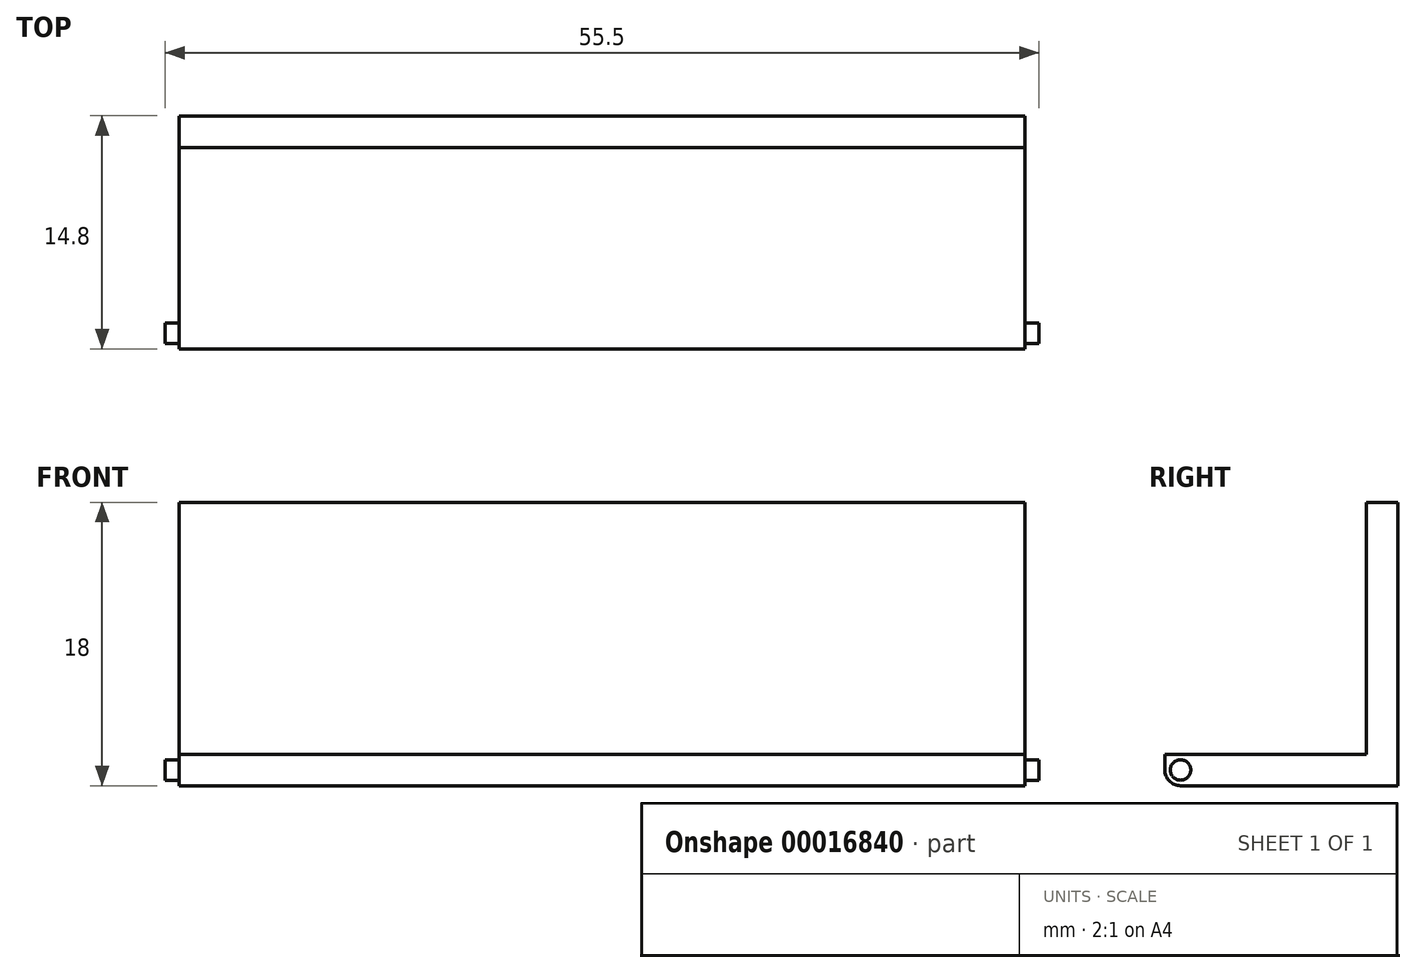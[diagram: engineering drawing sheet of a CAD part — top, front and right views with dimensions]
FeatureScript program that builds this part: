
annotation { "Feature Type Name" : "Feature", "Feature Type Description" : "" }
export const myFeature = defineFeature(function(context is Context, id is Id, definition is map)
    precondition{}
    {
        {
            var Q0;
            Q0=qCreatedBy(makeId("Top.planeOp"),FACE);
            var sketch = newSketch(context, id + "F0", { "sketchPlane" : qUnion([Q0])});
            skLineSegment(sketch, "E0.bottom", {"start": v(-78.46, -29.03) * mm, "end": v(-24.76, -29.03) * mm});
            skLineSegment(sketch, "E0.top", {"start": v(-78.46, -43.83) * mm, "end": v(-24.76, -43.83) * mm});
            skLineSegment(sketch, "E0.left", {"start": v(-78.46, -29.03) * mm, "end": v(-78.46, -43.83) * mm});
            skLineSegment(sketch, "E0.right", {"start": v(-24.76, -29.03) * mm, "end": v(-24.76, -43.83) * mm});
            skSolve(sketch);
        }
        {
            var Q0;
            Q0=makeQuery(id+"F0.imprint","IMPRINT",FACE,{"disambiguationData":[TD([[makeQuery(id+"F0.imprint","IMPRINT",EDGE,{"derivedFrom":sQuery(id+"F0.wireOp",EDGE,"E0.bottom")}),-1.0]])]});
            extrude(context, id + "F1", {"entities" : qUnion([Q0]), "depth" : 18 * mm});
        }
        {
            var Q0;
            Q0=makeQuery(id+"F1.opExtrude","CAP_FACE",FACE,{"disambiguationData":[OSD([sQuery(id+"F0.wireOp",EDGE,"E0.bottom"),sQuery(id+"F0.wireOp",EDGE,"E0.top"),sQuery(id+"F0.wireOp",EDGE,"E0.left"),sQuery(id+"F0.wireOp",EDGE,"E0.right")])],"isStart":false});
            shell(context, id + "F2", {"entities" : qUnion([Q0]), "thickness" : 2 * mm});
        }
        {
            var Q0;
            Q0=makeQuery(id+"F1.opExtrude","CAP_FACE",FACE,{"disambiguationData":[OSD([sQuery(id+"F0.wireOp",EDGE,"E0.bottom"),sQuery(id+"F0.wireOp",EDGE,"E0.top"),sQuery(id+"F0.wireOp",EDGE,"E0.left"),sQuery(id+"F0.wireOp",EDGE,"E0.right")])],"isStart":false});
            var sketch = newSketch(context, id + "F3", { "sketchPlane" : qUnion([Q0])});
            skLineSegment(sketch, "E1.bottom", {"start": v(-78.46, -31.03) * mm, "end": v(-24.76, -31.03) * mm});
            skLineSegment(sketch, "E1.top", {"start": v(-78.46, -43.83) * mm, "end": v(-24.76, -43.83) * mm});
            skLineSegment(sketch, "E1.left", {"start": v(-78.46, -31.03) * mm, "end": v(-78.46, -43.83) * mm});
            skLineSegment(sketch, "E1.right", {"start": v(-24.76, -31.03) * mm, "end": v(-24.76, -43.83) * mm});
            skSolve(sketch);
        }
        {
            var Q0;
            Q0 = qSketchRegion(id + "F3", true);
            extrude(context, id + "F4", {"entities" : qUnion([Q0]), "operationType" : NewBodyOperationType.REMOVE, "oppositeDirection" : true, "depth" : 16 * mm});
        }
        {
            var Q0;
            Q0=makeQuery(id+"F4.boolean.opBoolean","COPY",EDGE,{"derivedFrom":makeQuery(id+"F4.opExtrude","CAP_EDGE",EDGE,{"disambiguationData":[OSD([sQuery(id+"F3.wireOp",EDGE,"E1.top")])],"isStart":false})});
            var Q1;
            Q1=makeQuery(id+"F1.opExtrude","CAP_EDGE",EDGE,{"disambiguationData":[OSD([sQuery(id+"F0.wireOp",EDGE,"E0.top")])],"isStart":true});
            fillet(context, id + "F5", {"entities" : qUnion([Q0, Q1]), "radius" : 1 * mm, "tangentPropagation" : true, "allowEdgeOverflow" : false});
        }
        {
            var Q0;
            Q0=makeQuery(id+"F1.opExtrude","SWEPT_FACE",FACE,{"disambiguationData":[OSD([sQuery(id+"F0.wireOp",EDGE,"E0.left")])]});
            var sketch = newSketch(context, id + "F6", { "sketchPlane" : qUnion([Q0])});
            skCircle(sketch, "E2", {"center": v(42.83, 1) * mm, "radius": 0.65 * mm});
            skSolve(sketch);
        }
        {
            var Q0;
            Q0 = qSketchRegion(id + "F6", true);
            extrude(context, id + "F7", {"entities" : qUnion([Q0]), "operationType" : NewBodyOperationType.ADD, "depth" : 0.9 * mm});
        }
        {
            var Q0;
            Q0=makeQuery(id+"F1.opExtrude","SWEPT_FACE",FACE,{"disambiguationData":[OSD([sQuery(id+"F0.wireOp",EDGE,"E0.right")])]});
            var sketch = newSketch(context, id + "F8", { "sketchPlane" : qUnion([Q0])});
            skCircle(sketch, "E3", {"center": v(-42.83, 1) * mm, "radius": 0.65 * mm});
            skSolve(sketch);
        }
        {
            var Q0;
            Q0 = qSketchRegion(id + "F8", true);
            extrude(context, id + "F9", {"entities" : qUnion([Q0]), "operationType" : NewBodyOperationType.ADD, "depth" : 0.9 * mm});
        }
    });
